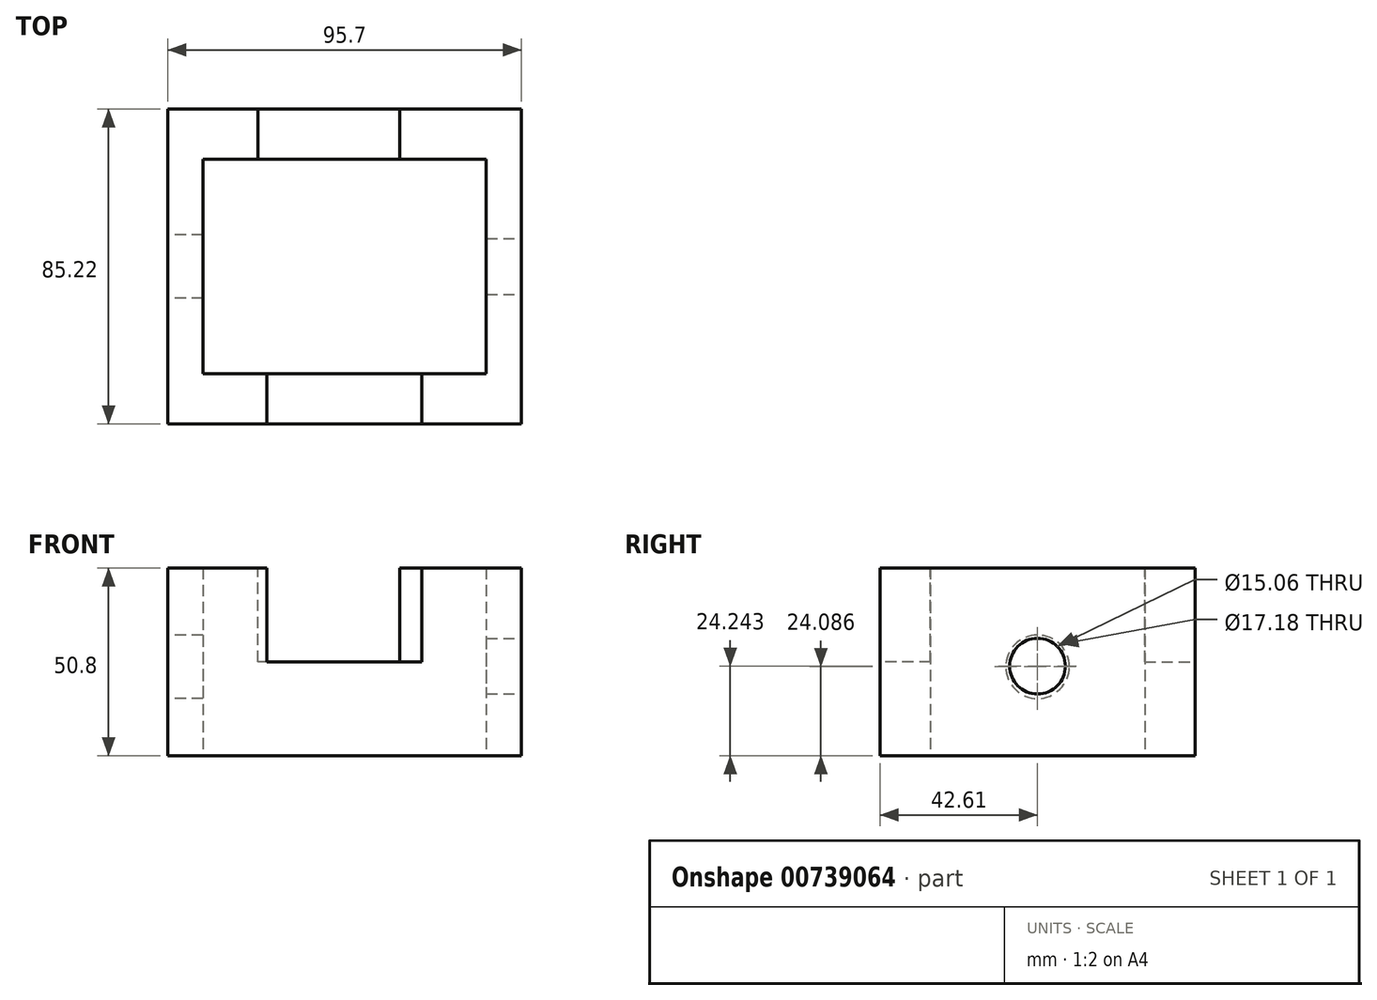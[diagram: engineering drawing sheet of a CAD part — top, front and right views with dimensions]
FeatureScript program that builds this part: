
annotation { "Feature Type Name" : "Feature", "Feature Type Description" : "" }
export const myFeature = defineFeature(function(context is Context, id is Id, definition is map)
    precondition{}
    {
        {
            var Q0;
            Q0=qCreatedBy(makeId("Top.planeOp"),FACE);
            var sketch = newSketch(context, id + "F0", { "sketchPlane" : qUnion([Q0])});
            skLineSegment(sketch, "E0.bottom", {"start": v(47.85, -42.61) * mm, "end": v(-47.85, -42.61) * mm});
            skLineSegment(sketch, "E0.top", {"start": v(47.85, 42.61) * mm, "end": v(-47.85, 42.61) * mm});
            skLineSegment(sketch, "E0.left", {"start": v(47.85, -42.61) * mm, "end": v(47.85, 42.61) * mm});
            skLineSegment(sketch, "E0.right", {"start": v(-47.85, -42.61) * mm, "end": v(-47.85, 42.61) * mm});
            skPoint(sketch, "E0.middle", {"position": v(0, 0) * mm});
            skLineSegment(sketch, "E1.bottom", {"start": v(38.33, -28.98) * mm, "end": v(-38.33, -28.98) * mm});
            skLineSegment(sketch, "E1.top", {"start": v(38.33, 28.98) * mm, "end": v(-38.33, 28.98) * mm});
            skLineSegment(sketch, "E1.left", {"start": v(38.33, -28.98) * mm, "end": v(38.33, 28.98) * mm});
            skLineSegment(sketch, "E1.right", {"start": v(-38.33, -28.98) * mm, "end": v(-38.33, 28.98) * mm});
            skSolve(sketch);
        }
        {
            var Q0;
            Q0 = qSketchRegion(id + "F0", true);
            extrude(context, id + "F1", {"entities" : qUnion([Q0]), "depth" : 50.8 * mm, "offsetDistance" : 25.4 * mm});
        }
        {
            var Q0;
            Q0=makeQuery(id+"F1.opExtrude","CAP_FACE",FACE,{"disambiguationData":[OSD([sQuery(id+"F0.wireOp",EDGE,"E0.bottom"),sQuery(id+"F0.wireOp",EDGE,"E0.top"),sQuery(id+"F0.wireOp",EDGE,"E0.left"),sQuery(id+"F0.wireOp",EDGE,"E0.right"),sQuery(id+"F0.wireOp",EDGE,"E1.bottom"),sQuery(id+"F0.wireOp",EDGE,"E1.top"),sQuery(id+"F0.wireOp",EDGE,"E1.left"),sQuery(id+"F0.wireOp",EDGE,"E1.right")])],"isStart":false});
            var sketch = newSketch(context, id + "F2", { "sketchPlane" : qUnion([Q0])});
            skLineSegment(sketch, "E2", {"start": v(-21.02, -28.98) * mm, "end": v(-21.02, -42.61) * mm});
            skLineSegment(sketch, "E3", {"start": v(20.88, -28.98) * mm, "end": v(20.88, -42.61) * mm});
            skSolve(sketch);
        }
        {
            var Q0;
            {var subQ0=sQuery(id+"F2.wireOp",EDGE,"E2");Q0=makeQuery(id+"F2.imprint","IMPRINT",FACE,{"disambiguationData":[TD([[makeQuery(id+"F2.imprint","IMPRINT",EDGE,{"derivedFrom":subQ0}),1.0]])]});}
            var sketch = newSketch(context, id + "F3", { "sketchPlane" : qUnion([Q0])});
            skSolve(sketch);
        }
        {
            var Q0;
            Q0 = qSketchRegion(id + "F3", true);
            var Q1;
            {var subQ0=sQuery(id+"F2.wireOp",EDGE,"E2");Q1=makeQuery(id+"F2.imprint","IMPRINT",FACE,{"disambiguationData":[TD([[makeQuery(id+"F2.imprint","IMPRINT",EDGE,{"derivedFrom":subQ0}),1.0]])]});}
            extrude(context, id + "F4", {"entities" : qUnion([Q0, Q1]), "operationType" : NewBodyOperationType.REMOVE, "oppositeDirection" : true, "depth" : 25.4 * mm, "offsetDistance" : 25.4 * mm});
        }
        {
            var Q0;
            Q0=makeQuery(id+"F1.opExtrude","CAP_FACE",FACE,{"disambiguationData":[OSD([sQuery(id+"F0.wireOp",EDGE,"E0.bottom"),sQuery(id+"F0.wireOp",EDGE,"E0.top"),sQuery(id+"F0.wireOp",EDGE,"E0.left"),sQuery(id+"F0.wireOp",EDGE,"E0.right"),sQuery(id+"F0.wireOp",EDGE,"E1.bottom"),sQuery(id+"F0.wireOp",EDGE,"E1.top"),sQuery(id+"F0.wireOp",EDGE,"E1.left"),sQuery(id+"F0.wireOp",EDGE,"E1.right")])],"isStart":false});
            var sketch = newSketch(context, id + "F5", { "sketchPlane" : qUnion([Q0])});
            skLineSegment(sketch, "E4", {"start": v(-23.47, 28.98) * mm, "end": v(-23.47, 42.61) * mm});
            skLineSegment(sketch, "E5", {"start": v(14.89, 28.98) * mm, "end": v(14.89, 42.61) * mm});
            skSolve(sketch);
        }
        {
            var Q0;
            Q0 = qSketchRegion(id + "F5", true);
            var Q1;
            {var subQ0=sQuery(id+"F5.wireOp",EDGE,"E4");Q1=makeQuery(id+"F5.imprint","IMPRINT",FACE,{"disambiguationData":[TD([[makeQuery(id+"F5.imprint","IMPRINT",EDGE,{"derivedFrom":subQ0}),-1.0]])]});}
            extrude(context, id + "F6", {"entities" : qUnion([Q0, Q1]), "operationType" : NewBodyOperationType.REMOVE, "oppositeDirection" : true, "depth" : 25.4 * mm, "offsetDistance" : 25.4 * mm});
        }
        {
            var Q0;
            Q0=makeQuery(id+"F1.opExtrude","SWEPT_FACE",FACE,{"disambiguationData":[OSD([sQuery(id+"F0.wireOp",EDGE,"E0.left")])]});
            var sketch = newSketch(context, id + "F7", { "sketchPlane" : qUnion([Q0])});
            skCircle(sketch, "E6", {"center": v(0, 24.24) * mm, "radius": 7.53 * mm});
            skSolve(sketch);
        }
        {
            var Q0;
            Q0=makeQuery(id+"F7.imprint","IMPRINT",FACE,{"disambiguationData":[TD([[makeQuery(id+"F7.imprint","IMPRINT",EDGE,{"derivedFrom":sQuery(id+"F7.wireOp",EDGE,"E6")}),1.0]])]});
            extrude(context, id + "F8", {"entities" : qUnion([Q0]), "operationType" : NewBodyOperationType.REMOVE, "oppositeDirection" : true, "depth" : 38.1 * mm, "offsetDistance" : 25.4 * mm});
        }
        {
            var Q0;
            Q0=makeQuery(id+"F1.opExtrude","SWEPT_FACE",FACE,{"disambiguationData":[OSD([sQuery(id+"F0.wireOp",EDGE,"E0.right")])]});
            var sketch = newSketch(context, id + "F9", { "sketchPlane" : qUnion([Q0])});
            skCircle(sketch, "E7", {"center": v(0, 24.43) * mm, "radius": 7.9 * mm});
            skSolve(sketch);
        }
        {
            var Q0;
            Q0=makeQuery(id+"F9.imprint","IMPRINT",FACE,{"disambiguationData":[TD([[makeQuery(id+"F9.imprint","IMPRINT",EDGE,{"derivedFrom":sQuery(id+"F9.wireOp",EDGE,"E7")}),1.0]])]});
            extrude(context, id + "F10", {"entities" : qUnion([Q0]), "operationType" : NewBodyOperationType.REMOVE, "depth" : 38.1 * mm, "offsetDistance" : 25.4 * mm});
        }
        {
            var Q0;
            Q0=makeQuery(id+"F1.opExtrude","SWEPT_FACE",FACE,{"disambiguationData":[OSD([sQuery(id+"F0.wireOp",EDGE,"E0.right")])]});
            var sketch = newSketch(context, id + "F11", { "sketchPlane" : qUnion([Q0])});
            skCircle(sketch, "E8", {"center": v(0, 24.09) * mm, "radius": 8.6 * mm});
            skSolve(sketch);
        }
        {
            var Q0;
            Q0 = qSketchRegion(id + "F11", true);
            extrude(context, id + "F12", {"entities" : qUnion([Q0]), "operationType" : NewBodyOperationType.REMOVE, "oppositeDirection" : true, "depth" : 25.4 * mm, "offsetDistance" : 25.4 * mm});
        }
    });
